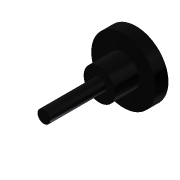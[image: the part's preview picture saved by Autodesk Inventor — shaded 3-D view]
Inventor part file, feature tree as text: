
AUTODESK INVENTOR PART (.ipt)
format: ipt  version: 2014 (Build 180170000, 170)  size: 83,456 bytes
history: native  units: mm
features: revolve x1, sketch x1
ambient origin geometry x8: Origin, YZ Plane, XZ Plane, XY Plane, X Axis, Y Axis, Z Axis, Center Point
bodies: Solid1 (feature_tree)
feature tree (2):
  revolve  "Revolution1"  [1 undecoded]
  sketch  "Sketch1"  dims[d0=25.5mm d1=10.0mm d2=19.0mm d3=12.5mm d4=44.0mm d5=5.0mm d6=90.0deg]
note: 1 required parameter value undecoded (feature->parameter linkage not recoverable at this tier; creation-order binding heuristic only, values carry confidence <= 0.55)
